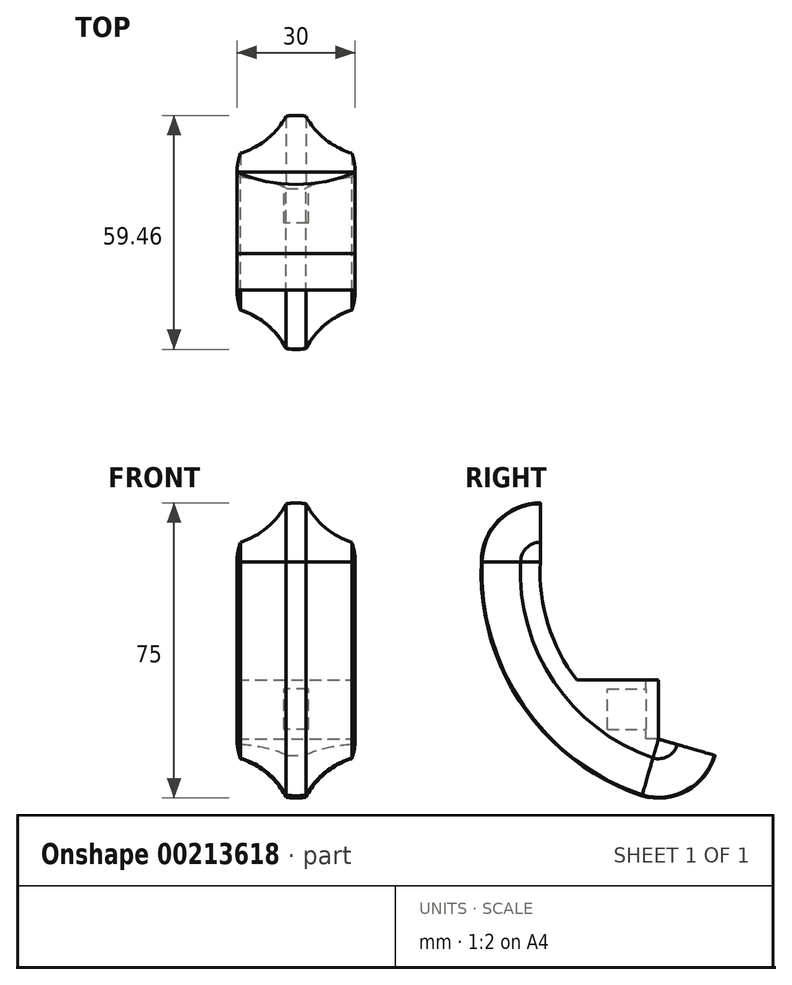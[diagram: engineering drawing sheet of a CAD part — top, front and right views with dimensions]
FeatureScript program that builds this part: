
annotation { "Feature Type Name" : "Feature", "Feature Type Description" : "" }
export const myFeature = defineFeature(function(context is Context, id is Id, definition is map)
    precondition{}
    {
        {
            var Q0;
            Q0=qCreatedBy(makeId("Right.planeOp"),FACE);
            var sketch = newSketch(context, id + "F0", { "sketchPlane" : qUnion([Q0])});
            skPoint(sketch, "E0", {"position": v(-30, 45) * mm});
            skPoint(sketch, "E1", {"position": v(0, 0) * mm});
            skArc(sketch, "E2", {"start": v(-30, 45) * mm, "mid": v(-22.51, 17.5) * mm, "end": v(0, 0) * mm});
            skSolve(sketch);
        }
        {
            var Q0;
            Q0=sQuery(id+"F0.wireOp",VERTEX,"E2.start");
            var Q1;
            Q1=qCreatedBy(makeId("Top.planeOp"),FACE);
            cPlane(context, id + "F1", {"entities" : qUnion([Q0, Q1]), "cplaneType" : CPlaneType.PLANE_POINT, "offset" : 25 * mm, "width" : 150 * mm, "height" : 150 * mm});
        }
        {
            var Q0;
            Q0=qCreatedBy(id+"F1.planeOp",FACE);
            var sketch = newSketch(context, id + "F2", { "sketchPlane" : qUnion([Q0])});
            skCircle(sketch, "E3", {"center": v(0, -30) * mm, "radius": 15 * mm});
            skLineSegment(sketch, "E4", {"start": v(-15, -30) * mm, "end": v(15, -30) * mm});
            skArc(sketch, "E5", {"start": v(-2.5, -44.8) * mm, "mid": v(-7.35, -38.75) * mm, "end": v(-14.14, -35) * mm});
            skLineSegment(sketch, "E6", {"start": v(0, -30) * mm, "end": v(0, -45) * mm, "construction": true});
            skArc(sketch, "E7.MirrorCS", {"start": v(2.5, -44.8) * mm, "mid": v(7.35, -38.75) * mm, "end": v(14.14, -35) * mm});
            skSolve(sketch);
        }
        {
            var Q0;
            {var subQ0=sQuery(id+"F2.wireOp",EDGE,"E4");Q0=makeQuery(id+"F2.imprint","IMPRINT",FACE,{"disambiguationData":[TD([[makeQuery(id+"F2.imprint","IMPRINT",EDGE,{"derivedFrom":subQ0}),-1.0]])]});}
            var Q1;
            Q1=sQuery(id+"F0.wireOp",EDGE,"E2");
            sweep(context, id + "F3", {"profiles" : qUnion([Q0]), "path" : qUnion([Q1])});
        }
        {
            var Q0;
            Q0=makeQuery(id+"F3.opSweep","CAP_FACE",FACE,{"disambiguationData":[OSD([sQuery(id+"F0.wireOp",VERTEX,"E2.end"),sQuery(id+"F2.wireOp",EDGE,"E3"),sQuery(id+"F2.wireOp",EDGE,"E4"),sQuery(id+"F2.wireOp",EDGE,"E5"),sQuery(id+"F2.wireOp",EDGE,"E7.MirrorCS")])],"isStart":false});
            var Q1;
            Q1=makeQuery(id+"F3.opSweep","CAP_EDGE",EDGE,{"disambiguationData":[OSD([sQuery(id+"F0.wireOp",VERTEX,"E2.end"),sQuery(id+"F2.wireOp",EDGE,"E4")])],"isStart":false});
            revolve(context, id + "F4", {"operationType" : NewBodyOperationType.ADD, "entities" : qUnion([Q0]), "axis" : qUnion([Q1]), "revolveType" : RevolveType.ONE_DIRECTION, "angle" : 90 * degree});
        }
        {
            var Q0;
            Q0=makeQuery(id+"F3.opSweep","CAP_FACE",FACE,{"disambiguationData":[OSD([sQuery(id+"F0.wireOp",VERTEX,"E2.start"),sQuery(id+"F2.wireOp",EDGE,"E3"),sQuery(id+"F2.wireOp",EDGE,"E4"),sQuery(id+"F2.wireOp",EDGE,"E5"),sQuery(id+"F2.wireOp",EDGE,"E7.MirrorCS")])],"isStart":true});
            var Q1;
            Q1=makeQuery(id+"F3.opSweep","CAP_EDGE",EDGE,{"disambiguationData":[OSD([sQuery(id+"F0.wireOp",VERTEX,"E2.start"),sQuery(id+"F2.wireOp",EDGE,"E4")])],"isStart":true});
            revolve(context, id + "F5", {"operationType" : NewBodyOperationType.ADD, "entities" : qUnion([Q0]), "axis" : qUnion([Q1]), "revolveType" : RevolveType.ONE_DIRECTION, "oppositeDirection" : true, "angle" : 90 * degree});
        }
        {
            var Q0;
            Q0=qCreatedBy(makeId("Front.planeOp"),FACE);
            var Q1;
            {var subQ0=sQuery(id+"F2.wireOp",EDGE,"E4");var subQ1=sQuery(id+"F2.wireOp",EDGE,"E3");var subQ2=sQuery(id+"F0.wireOp",EDGE,"E2");var subQ3=makeQuery(id+"F3.opSweep","CAP_VERTEX",VERTEX,{"disambiguationData":[OSD([subQ2,subQ1,subQ0]),TDD([subQ2,makeQuery(id+"F2.imprint","INTERSECT",VERTEX,{"disambiguationData":[OD(1.0)],"derivedFrom":[subQ1,subQ0]})])],"isStart":false});Q1=makeQuery(id+"F4.boolean.opBoolean","MERGE",VERTEX,{"derivedFrom":[subQ3,makeQuery(id+"F4.opRevolve","CAP_VERTEX",VERTEX,{"disambiguationData":[OSD([subQ2,subQ1,subQ0]),TDD([subQ3])],"isStart":true})]});}
            cPlane(context, id + "F6", {"entities" : qUnion([Q0, Q1]), "cplaneType" : CPlaneType.PLANE_POINT, "offset" : 25 * mm, "width" : 150 * mm, "height" : 150 * mm});
        }
        {
            var Q0;
            Q0=qCreatedBy(id+"F6.planeOp",FACE);
            var sketch = newSketch(context, id + "F7", { "sketchPlane" : qUnion([Q0])});
            skLineSegment(sketch, "E8.bottom", {"start": v(15, 15) * mm, "end": v(-15, 15) * mm});
            skLineSegment(sketch, "E8.left", {"start": v(15, 15) * mm, "end": v(15, 0) * mm});
            skLineSegment(sketch, "E8.right", {"start": v(-15, 15) * mm, "end": v(-15, 0) * mm});
            skPoint(sketch, "E8.middle", {"position": v(0, 0) * mm});
            skLineSegment(sketch, "E9", {"start": v(15, 0) * mm, "end": v(-15, 0) * mm});
            skPoint(sketch, "E8.top.end.orphan", {"position": v(-15, -15) * mm});
            skPoint(sketch, "E10.orphan", {"position": v(15, -15) * mm});
            skSolve(sketch);
        }
        {
            var Q0;
            Q0 = qSketchRegion(id + "F7", true);
            var Q1;
            Q1=makeQuery(id+"F3.opSweep","SWEPT_FACE",FACE,{"disambiguationData":[OSD([sQuery(id+"F0.wireOp",EDGE,"E2"),sQuery(id+"F2.wireOp",EDGE,"E4")])]});
            extrude(context, id + "F8", {"entities" : qUnion([Q0]), "operationType" : NewBodyOperationType.ADD, "endBound" : BoundingType.UP_TO_SURFACE, "endBoundEntityFace" : qUnion([Q1]), "depth" : 25 * mm});
        }
        {
            var Q0;
            Q0=makeQuery(id+"F8.opExtrude","CAP_FACE",FACE,{"disambiguationData":[OSD([sQuery(id+"F7.wireOp",EDGE,"E8.bottom"),sQuery(id+"F7.wireOp",EDGE,"E8.left"),sQuery(id+"F7.wireOp",EDGE,"E8.right"),sQuery(id+"F7.wireOp",EDGE,"E9")])],"isStart":true});
            var sketch = newSketch(context, id + "F9", { "sketchPlane" : qUnion([Q0])});
            skLineSegment(sketch, "E11.bottom", {"start": v(-3.1, 2.5) * mm, "end": v(3.1, 2.5) * mm});
            skLineSegment(sketch, "E11.top", {"start": v(-3.1, 12.7) * mm, "end": v(3.1, 12.7) * mm});
            skLineSegment(sketch, "E11.left", {"start": v(-3.1, 2.5) * mm, "end": v(-3.1, 12.7) * mm});
            skLineSegment(sketch, "E11.right", {"start": v(3.1, 2.5) * mm, "end": v(3.1, 12.7) * mm});
            skPoint(sketch, "E11.middle", {"position": v(0, 7.6) * mm});
            skSolve(sketch);
        }
        {
            var Q0;
            Q0 = qSketchRegion(id + "F9", true);
            extrude(context, id + "F10", {"entities" : qUnion([Q0]), "operationType" : NewBodyOperationType.REMOVE, "oppositeDirection" : true, "depth" : 13 * mm});
        }
        {
            var Q0;
            Q0=makeQuery(id+"F8.opExtrude","SWEPT_FACE",FACE,{"disambiguationData":[OSD([sQuery(id+"F7.wireOp",EDGE,"E8.bottom")])]});
            var sketch = newSketch(context, id + "F11", { "sketchPlane" : qUnion([Q0])});
            skLineSegment(sketch, "E12", {"start": v(-15, 0) * mm, "end": v(15, 0) * mm});
            skArc(sketch, "E13", {"start": v(-15, 0) * mm, "mid": v(0, -3.13) * mm, "end": v(15, 0) * mm});
            skSolve(sketch);
        }
        {
            var Q0;
            Q0 = qSketchRegion(id + "F11", true);
            extrude(context, id + "F12", {"entities" : qUnion([Q0]), "operationType" : NewBodyOperationType.REMOVE, "oppositeDirection" : true, "depth" : 15 * mm});
        }
    });
